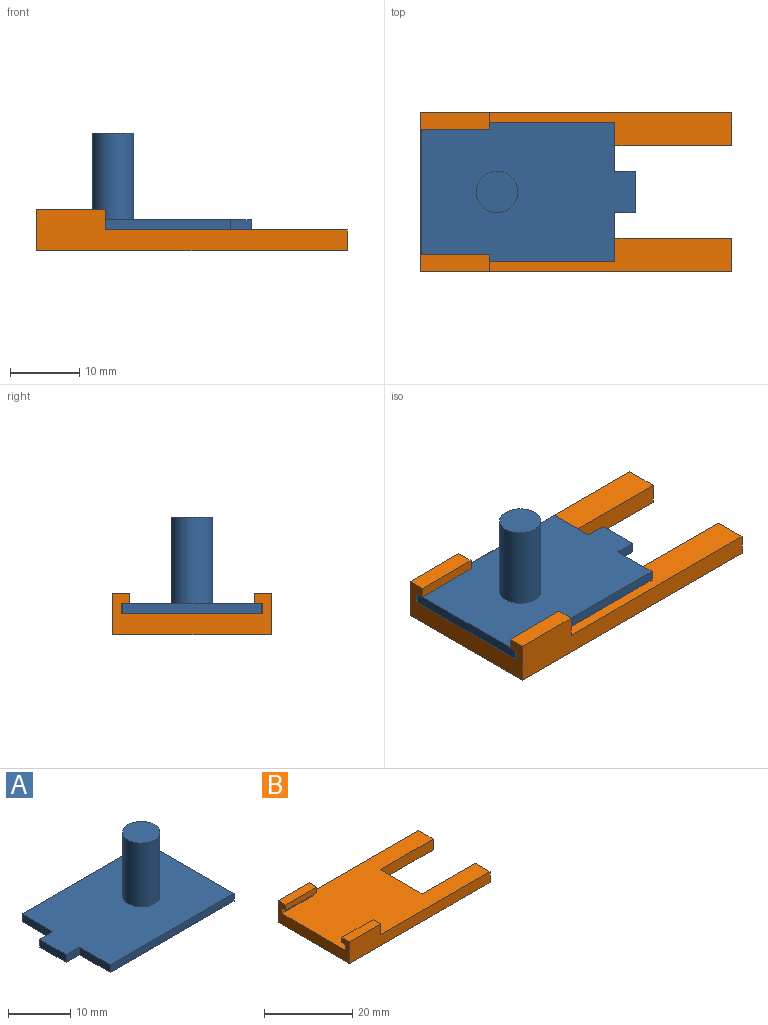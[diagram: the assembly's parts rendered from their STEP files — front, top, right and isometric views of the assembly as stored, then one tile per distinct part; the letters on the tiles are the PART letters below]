
ASSEMBLY  parts=2 mates=1
PART A: 12 faces, bbox 31x20x14 mm
  f0: plane 7x1.5mm, normal (-1,0,0), area 10.5mm2, adj f1,f7,f8,f9
  f1: plane 3x1.5mm, normal (0,1,0), area 4.5mm2, adj f0,f2,f8,f9
  f2: plane 6x1.5mm, normal (-1,0,0), area 9mm2, adj f1,f3,f8,f9
  f3: plane 3x1.5mm, normal (0,-1,0), area 4.5mm2, adj f2,f4,f8,f9
  f4: plane 7x1.5mm, normal (-1,0,0), area 10.5mm2, adj f3,f5,f8,f9
  f5: plane 28x1.5mm, normal (0,-1,0), area 42mm2, adj f4,f6,f8,f9
  f6: plane 20x1.5mm, normal (1,0,0), area 30mm2, adj f5,f7,f8,f9
  f7: plane 28x1.5mm, normal (0,1,0), area 42mm2, adj f0,f6,f8,f9
  f8: plane 31x20mm, normal (0,0,1), area 549.7mm2, adj f0,f1,f2,f3,f4,f5,f6,f7
  f9: plane 31x20mm, normal (0,0,-1), area 578mm2, adj f0,f1,f2,f3,f4,f5,f6,f7
  f10: cylinder r=3mm len=12.5mm, axis (0,0,-1), area 235.6mm2, adj f8,f11
  f11: plane 6x6mm, normal (0,0,1), area 28.3mm2, adj f10
PART B: 20 faces, bbox 45x23x6 mm
  f0: plane 10x1.5mm, normal (0,-1,0), area 15mm2, adj f1,f4,f14,f18
  f1: plane 3x2.5mm, normal (1,0,0), area 5.6mm2, adj f0,f5,f12,f14,f18,f19
  f2: plane 10x1.5mm, normal (0,1,0), area 15mm2, adj f3,f4,f15,f17
  f3: plane 3x2.5mm, normal (1,0,0), area 5.6mm2, adj f2,f5,f6,f15,f16,f17
  f4: plane 23x6mm, normal (-1,0,0), area 80.2mm2, adj f0,f2,f5,f6,f12,f13,f14,f15
  f5: plane 45x23mm, normal (0,0,1), area 782.2mm2, adj f1,f3,f4,f6,f7,f8,f9,f10
  f6: plane 45x6mm, normal (0,-1,0), area 165mm2, adj f3,f4,f5,f7,f13,f15
  f7: plane 4.8x3mm, normal (1,0,0), area 14.4mm2, adj f5,f6,f8,f13
  f8: plane 17x3mm, normal (0,1,0), area 51mm2, adj f5,f7,f9,f13
  f9: plane 13.4x3mm, normal (1,0,0), area 40.2mm2, adj f5,f8,f10,f13
  f10: plane 17x3mm, normal (0,-1,0), area 51mm2, adj f5,f9,f11,f13
  f11: plane 4.8x3mm, normal (1,0,0), area 14.4mm2, adj f5,f10,f12,f13
  f12: plane 45x6mm, normal (0,1,0), area 165mm2, adj f1,f4,f5,f11,f13,f14
  f13: plane 45x23mm, normal (0,0,-1), area 807.2mm2, adj f4,f6,f7,f8,f9,f10,f11,f12
  f14: plane 10x2.5mm, normal (0,0,1), area 25mm2, adj f0,f1,f4,f12
  f15: plane 10x2.5mm, normal (0,0,1), area 25mm2, adj f2,f3,f4,f6
  f16: plane 10x1.5mm, normal (0,1,0), area 15mm2, adj f3,f4,f5,f17
  f17: plane 10x1.25mm, normal (0,0,-1), area 12.5mm2, adj f2,f3,f4,f16
  f18: plane 10x1.25mm, normal (0,0,-1), area 12.5mm2, adj f0,f1,f4,f19
  f19: plane 10x1.5mm, normal (0,-1,0), area 15mm2, adj f1,f4,f5,f18
PLACE A rot(axis=(0,0,1),180deg) t=(-4.48,0,3)mm
PLACE B t=(3.95,0,0)mm
MATE planar A.f9 <-> B.f5  axis (0,0,-1) through (-4,0,3)mm
